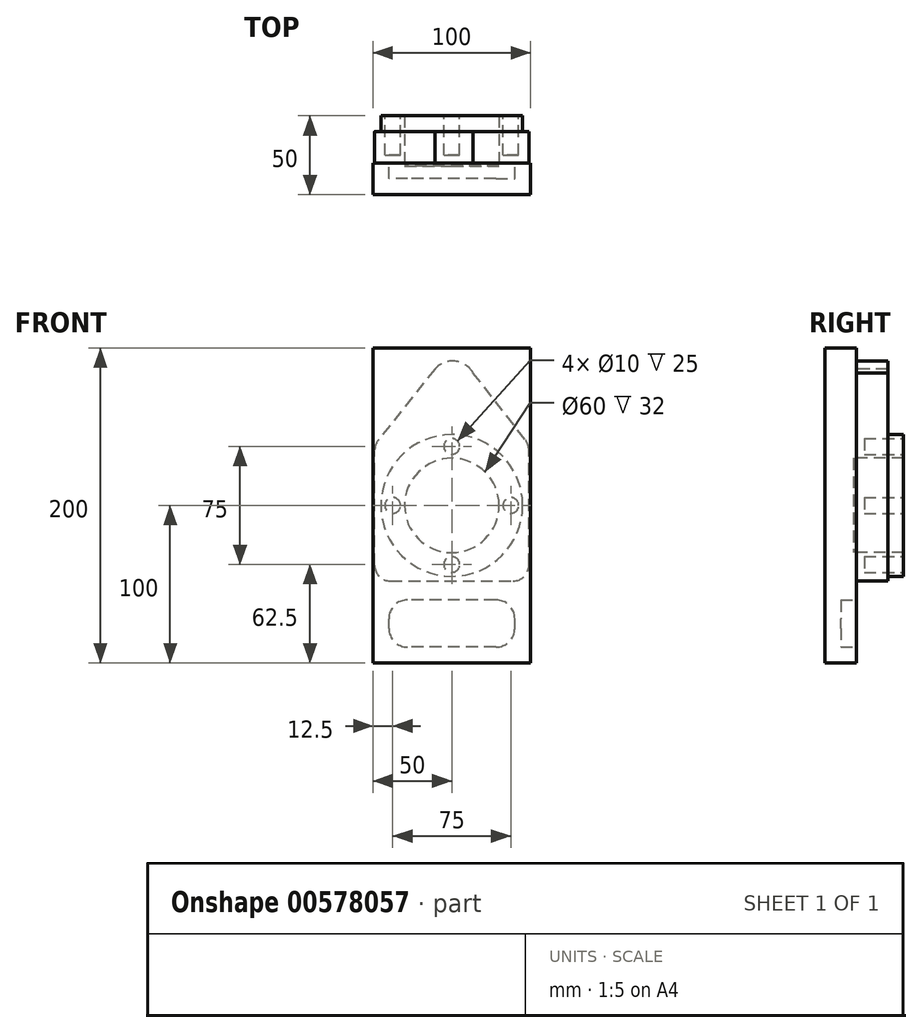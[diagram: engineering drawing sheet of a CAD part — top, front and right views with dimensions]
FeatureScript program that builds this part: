
annotation { "Feature Type Name" : "Feature", "Feature Type Description" : "" }
export const myFeature = defineFeature(function(context is Context, id is Id, definition is map)
    precondition{}
    {
        {
            var Q0;
            Q0=qCreatedBy(makeId("Front.planeOp"),FACE);
            var sketch = newSketch(context, id + "F0", { "sketchPlane" : qUnion([Q0])});
            skLineSegment(sketch, "E0", {"start": v(0, 0) * mm, "end": v(0, -200) * mm});
            skLineSegment(sketch, "E1", {"start": v(0, -200) * mm, "end": v(100, -200) * mm});
            skLineSegment(sketch, "E2", {"start": v(100, -200) * mm, "end": v(100, 0) * mm});
            skLineSegment(sketch, "E3", {"start": v(0, 0) * mm, "end": v(100, 0) * mm});
            skSolve(sketch);
        }
        {
            var Q0;
            Q0 = qSketchRegion(id + "F0", true);
            extrude(context, id + "F1", {"entities" : qUnion([Q0]), "depth" : 20 * mm, "offsetDistance" : 25 * mm});
        }
        {
            var Q0;
            Q0=makeQuery(id+"F1.opExtrude","CAP_FACE",FACE,{"disambiguationData":[OSD([sQuery(id+"F0.wireOp",EDGE,"E0"),sQuery(id+"F0.wireOp",EDGE,"E1"),sQuery(id+"F0.wireOp",EDGE,"E2"),sQuery(id+"F0.wireOp",EDGE,"E3")])],"isStart":true});
            var sketch = newSketch(context, id + "F2", { "sketchPlane" : qUnion([Q0])});
            skLineSegment(sketch, "E4.bottom", {"start": v(-78, -190) * mm, "end": v(-22, -190) * mm});
            skLineSegment(sketch, "E4.top", {"start": v(-78, -160) * mm, "end": v(-22, -160) * mm});
            skLineSegment(sketch, "E4.left", {"start": v(-90, -178) * mm, "end": v(-90, -172) * mm});
            skLineSegment(sketch, "E4.right", {"start": v(-10, -178) * mm, "end": v(-10, -172) * mm});
            skPoint(sketch, "E5.visualSharp", {"position": v(-90, -190) * mm});
            skArc(sketch, "E5.filletArc", {"start": v(-90, -178) * mm, "mid": v(-86.49, -186.49) * mm, "end": v(-78, -190) * mm});
            skPoint(sketch, "E6.visualSharp", {"position": v(-90, -160) * mm});
            skArc(sketch, "E6.filletArc", {"start": v(-78, -160) * mm, "mid": v(-86.49, -163.51) * mm, "end": v(-90, -172) * mm});
            skPoint(sketch, "E7.visualSharp", {"position": v(-10, -160) * mm});
            skArc(sketch, "E7.filletArc", {"start": v(-10, -172) * mm, "mid": v(-13.51, -163.51) * mm, "end": v(-22, -160) * mm});
            skPoint(sketch, "E8.visualSharp", {"position": v(-10, -190) * mm});
            skArc(sketch, "E8.filletArc", {"start": v(-22, -190) * mm, "mid": v(-13.51, -186.49) * mm, "end": v(-10, -178) * mm});
            skSolve(sketch);
        }
        {
            var Q0;
            Q0 = qSketchRegion(id + "F2", true);
            extrude(context, id + "F3", {"entities" : qUnion([Q0]), "operationType" : NewBodyOperationType.REMOVE, "oppositeDirection" : true, "depth" : 10 * mm, "offsetDistance" : 25 * mm});
        }
        {
            var Q0;
            Q0=makeQuery(id+"F1.opExtrude","CAP_FACE",FACE,{"disambiguationData":[OSD([sQuery(id+"F0.wireOp",EDGE,"E0"),sQuery(id+"F0.wireOp",EDGE,"E1"),sQuery(id+"F0.wireOp",EDGE,"E2"),sQuery(id+"F0.wireOp",EDGE,"E3")])],"isStart":true});
            var sketch = newSketch(context, id + "F4", { "sketchPlane" : qUnion([Q0])});
            skLineSegment(sketch, "E9", {"start": v(0, -200) * mm, "end": v(0, -148) * mm, "construction": true});
            skLineSegment(sketch, "E10", {"start": v(0, -148) * mm, "end": v(-1, -148) * mm, "construction": true});
            skLineSegment(sketch, "E11", {"start": v(-11, -148) * mm, "end": v(-89, -148) * mm});
            skLineSegment(sketch, "E12", {"start": v(-99, -138) * mm, "end": v(-99, -65.36) * mm});
            skLineSegment(sketch, "E13", {"start": v(-1, -138) * mm, "end": v(-1, -65.45) * mm});
            skPoint(sketch, "E14.visualSharp", {"position": v(-99, -148) * mm});
            skArc(sketch, "E14.filletArc", {"start": v(-99, -138) * mm, "mid": v(-96.07, -145.07) * mm, "end": v(-89, -148) * mm});
            skPoint(sketch, "E15.visualSharp", {"position": v(-1, -148) * mm});
            skArc(sketch, "E15.filletArc", {"start": v(-11, -148) * mm, "mid": v(-3.93, -145.07) * mm, "end": v(-1, -138) * mm});
            skPoint(sketch, "E16.visualSharp", {"position": v(-99, -71.24) * mm});
            skPoint(sketch, "E17.visualSharp", {"position": v(-1, -71.24) * mm});
            skPoint(sketch, "E18.visualSharp", {"position": v(-59.8, -12.88) * mm});
            skArc(sketch, "E18.filletArc", {"start": v(-39.4, -13.24) * mm, "mid": v(-52.12, -8.32) * mm, "end": v(-63.57, -15.75) * mm});
            skLineSegment(sketch, "E19", {"start": v(-96.47, -57.99) * mm, "end": v(-63.57, -15.75) * mm});
            skLineSegment(sketch, "E20", {"start": v(-39.4, -13.24) * mm, "end": v(-3.63, -57.95) * mm});
            skPoint(sketch, "E21.visualSharp", {"position": v(-99, -61.24) * mm});
            skArc(sketch, "E21.filletArc", {"start": v(-96.47, -57.99) * mm, "mid": v(-98.35, -61.46) * mm, "end": v(-99, -65.36) * mm});
            skPoint(sketch, "E22.visualSharp", {"position": v(-1, -61.24) * mm});
            skArc(sketch, "E22.filletArc", {"start": v(-1, -65.45) * mm, "mid": v(-1.68, -61.48) * mm, "end": v(-3.63, -57.95) * mm});
            skSolve(sketch);
        }
        {
            var Q0;
            Q0 = qSketchRegion(id + "F4", true);
            extrude(context, id + "F5", {"entities" : qUnion([Q0]), "operationType" : NewBodyOperationType.ADD, "depth" : 20 * mm, "offsetDistance" : 25 * mm});
        }
        {
            var Q0;
            Q0=makeQuery(id+"F5.opExtrude","CAP_FACE",FACE,{"disambiguationData":[OSD([sQuery(id+"F4.wireOp",EDGE,"E11"),sQuery(id+"F4.wireOp",EDGE,"E12"),sQuery(id+"F4.wireOp",EDGE,"E13"),sQuery(id+"F4.wireOp",EDGE,"E14.filletArc"),sQuery(id+"F4.wireOp",EDGE,"E15.filletArc"),sQuery(id+"F4.wireOp",EDGE,"E18.filletArc"),sQuery(id+"F4.wireOp",EDGE,"E19"),sQuery(id+"F4.wireOp",EDGE,"E20"),sQuery(id+"F4.wireOp",EDGE,"E21.filletArc"),sQuery(id+"F4.wireOp",EDGE,"E22.filletArc")])],"isStart":false});
            var sketch = newSketch(context, id + "F6", { "sketchPlane" : qUnion([Q0])});
            skCircle(sketch, "E23", {"center": v(-50, -100) * mm, "radius": 30 * mm});
            skCircle(sketch, "E24", {"center": v(-50, -100) * mm, "radius": 45 * mm});
            skSolve(sketch);
        }
        {
            var Q0;
            Q0 = qSketchRegion(id + "F6", true);
            extrude(context, id + "F7", {"entities" : qUnion([Q0]), "operationType" : NewBodyOperationType.ADD, "depth" : 10 * mm, "offsetDistance" : 25 * mm});
        }
        {
            var Q0;
            Q0=makeQuery(id+"F7.boolean.opBoolean","SPLIT",FACE,{"disambiguationData":[TD([makeQuery(id+"F7.opExtrude","SWEPT_FACE",FACE,{"disambiguationData":[OSD([sQuery(id+"F6.wireOp",EDGE,"E23")])]})])],"derivedFrom":makeQuery(id+"F5.opExtrude","CAP_FACE",FACE,{"disambiguationData":[OSD([sQuery(id+"F4.wireOp",EDGE,"E11"),sQuery(id+"F4.wireOp",EDGE,"E12"),sQuery(id+"F4.wireOp",EDGE,"E13"),sQuery(id+"F4.wireOp",EDGE,"E14.filletArc"),sQuery(id+"F4.wireOp",EDGE,"E15.filletArc"),sQuery(id+"F4.wireOp",EDGE,"E18.filletArc"),sQuery(id+"F4.wireOp",EDGE,"E19"),sQuery(id+"F4.wireOp",EDGE,"E20"),sQuery(id+"F4.wireOp",EDGE,"E21.filletArc"),sQuery(id+"F4.wireOp",EDGE,"E22.filletArc")])],"isStart":false})});
            var sketch = newSketch(context, id + "F8", { "sketchPlane" : qUnion([Q0])});
            skCircle(sketch, "E25", {"center": v(-50, -100) * mm, "radius": 30 * mm});
            skSolve(sketch);
        }
        {
            var Q0;
            Q0 = qSketchRegion(id + "F8", true);
            extrude(context, id + "F9", {"entities" : qUnion([Q0]), "operationType" : NewBodyOperationType.REMOVE, "oppositeDirection" : true, "depth" : 22 * mm, "offsetDistance" : 25 * mm});
        }
        {
            var Q0;
            Q0=makeQuery(id+"F7.opExtrude","CAP_FACE",FACE,{"disambiguationData":[OSD([sQuery(id+"F6.wireOp",EDGE,"E23"),sQuery(id+"F6.wireOp",EDGE,"E24")])],"isStart":false});
            var sketch = newSketch(context, id + "F10", { "sketchPlane" : qUnion([Q0])});
            skCircle(sketch, "E26", {"center": v(-50, -100) * mm, "radius": 37.5 * mm, "construction": true});
            skCircle(sketch, "E27", {"center": v(-87.5, -100) * mm, "radius": 5 * mm});
            skCircle(sketch, "E28", {"center": v(-12.5, -100) * mm, "radius": 5 * mm});
            skCircle(sketch, "E29", {"center": v(-50, -137.5) * mm, "radius": 5 * mm});
            skCircle(sketch, "E30", {"center": v(-50, -62.5) * mm, "radius": 5 * mm});
            skSolve(sketch);
        }
        {
            var Q0;
            Q0 = qSketchRegion(id + "F10", true);
            extrude(context, id + "F11", {"entities" : qUnion([Q0]), "operationType" : NewBodyOperationType.REMOVE, "oppositeDirection" : true, "depth" : 25 * mm, "offsetDistance" : 25 * mm});
        }
    });
